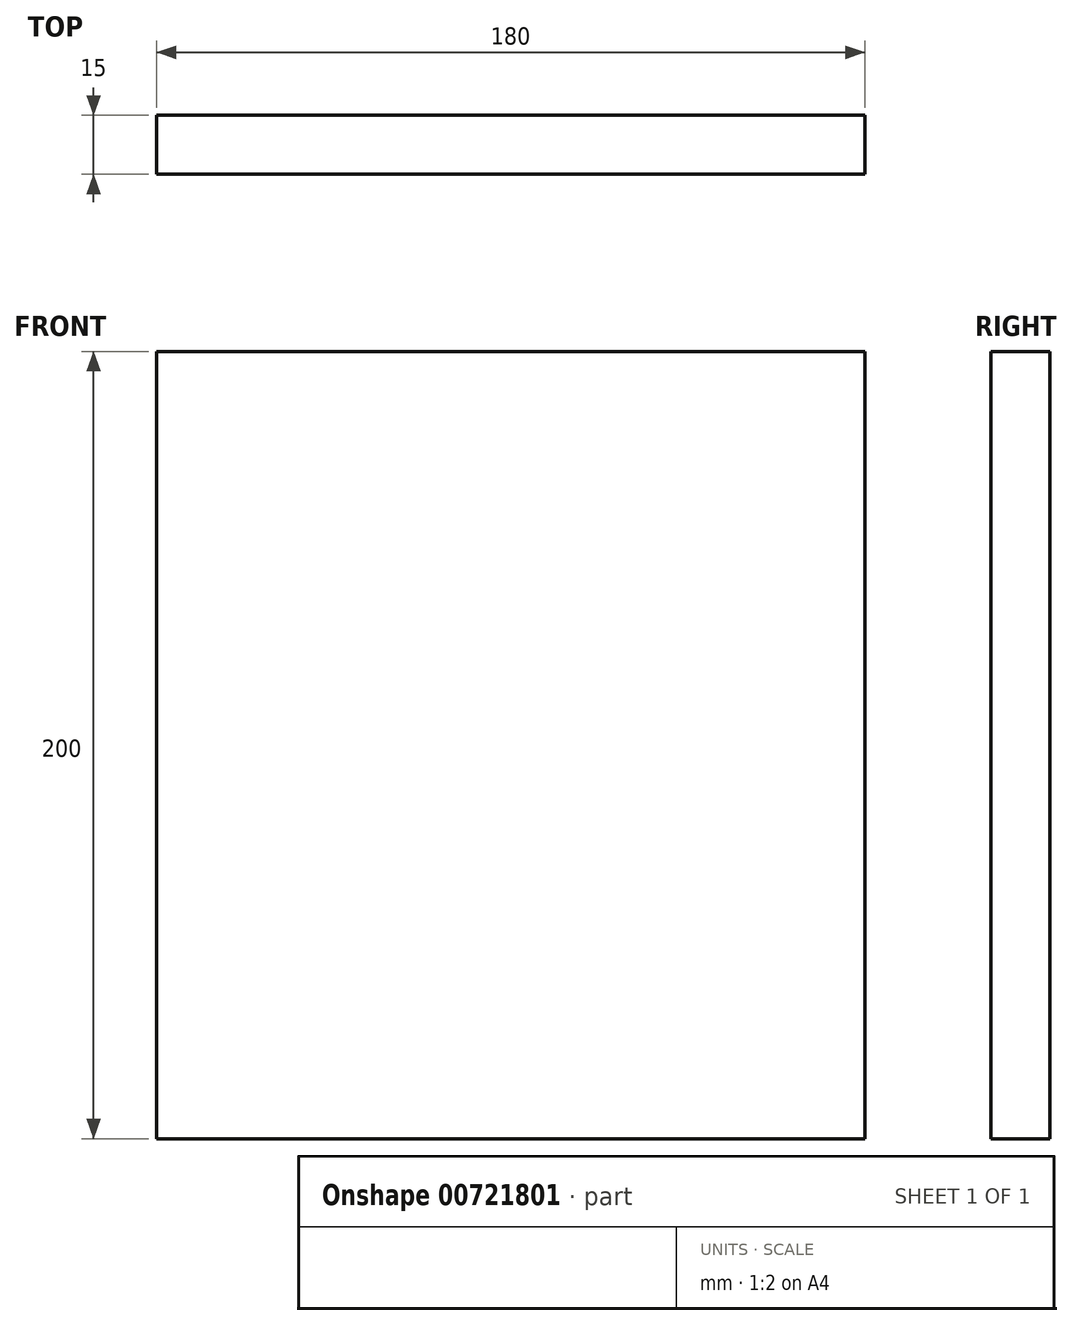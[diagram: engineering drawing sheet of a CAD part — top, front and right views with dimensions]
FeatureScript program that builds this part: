
annotation { "Feature Type Name" : "Feature", "Feature Type Description" : "" }
export const myFeature = defineFeature(function(context is Context, id is Id, definition is map)
    precondition{}
    {
        {
            var Q0;
            Q0=qCreatedBy(makeId("Front.planeOp"),FACE);
            var sketch = newSketch(context, id + "F0", { "sketchPlane" : qUnion([Q0])});
            skLineSegment(sketch, "E0.bottom", {"start": v(90, -100) * mm, "end": v(-90, -100) * mm});
            skLineSegment(sketch, "E0.top", {"start": v(90, 100) * mm, "end": v(-90, 100) * mm});
            skLineSegment(sketch, "E0.left", {"start": v(90, -100) * mm, "end": v(90, 100) * mm});
            skLineSegment(sketch, "E0.right", {"start": v(-90, -100) * mm, "end": v(-90, 100) * mm});
            skPoint(sketch, "E0.middle", {"position": v(0, 0) * mm});
            skSolve(sketch);
        }
        {
            var Q0;
            Q0 = qSketchRegion(id + "F0", true);
            extrude(context, id + "F1", {"entities" : qUnion([Q0]), "depth" : 15 * mm, "offsetDistance" : 25 * mm});
        }
    });
